# Revit family: Sunshade_Rectangular-CRL-Aluminum-Adjustable
name_source: partatom
category: Specialty Equipment
revit_build: Autodesk Revit 2016 (Build: 20150701_1515(x64)
units: mm (PartAtom-declared; Revit-internal decimal feet)

## family parameters
Always vertical = Yes
Cut with Voids When Loaded = No
OmniClass Number = 23.25.20.14.11.11
OmniClass Title = Curtain Wall Components
Part Type = Normal
Room Calculation Point = No
Round Connector Dimension = Use Diameter
Shared = No
Work Plane-Based = No

## types (5) — shared parameters
Assembly Code = B1020800
Description = rectangular outrigger with rectangular blades
Front Offset = 5"
Manufacturer = C.R. Laurence - U.S. Aluminum
Outrigger Count = 4
Product Documentation Link = http://www.crl-arch.com
Product Page URL = http://www.crlaurence.com
Rear Offset = 8"
URL = http://www.crl-arch.com

## per-type parameters (varying)
| type | Blade Count | Blade Length | Model | OA Width | Outrigger | bracket | infill blade |
| 30" projection 4 blades | 4 | 143 1/2" | sunshade components : AW0S2_6, AXRC1X6, AWSB5US6 | 144" | 29" | Sunshade_Outrigger-CRL_Rectangle_storefront | Sunshade_blade-CRL_AXRC1X6_Rec |
| 36" projection 5 blades | 5 | 119 1/2" | sunshade components : AW0S2_6, AXRC1X6, AWSB5US6 | 120" | 35" | Sunshade_Outrigger-CRL_Rectangle_wallmount | Sunshade_blade-CRL_AX06_airfoil |
| 42" projection 6 blades | 6 | 143 1/2" | sunshade components : AW0S2_6, AXRC1X6, AWSB5US6 | 144" | 41" | Sunshade_Outrigger-CRL_Rectangle_storefront | Sunshade_blade-CRL_AXRC1X6_Rec |
| 48" projection 7 blades | 7 | 143 1/2" | sunshade components : AW0S2_6, AXRC1X6, AWSB5US6 | 144" | 47" | Sunshade_Outrigger-CRL_Rectangle_storefront | Sunshade_blade-CRL_AXRC1X6_Rec |
| 24" projection 3 blades | 3 | 119 1/2" | components : AW0S2_6, AXRC1X6, AX06 AWSB5US6, AWSB1TC6 | 120" | 23" | Sunshade_Outrigger-CRL_Rectangle_storefront | Sunshade_blade-CRL_AXRC1X6_Rec |

## geometry (parser evidence)
native form markers: Blend x2, Sweep x25
no freeform markers — native parametric forms only
